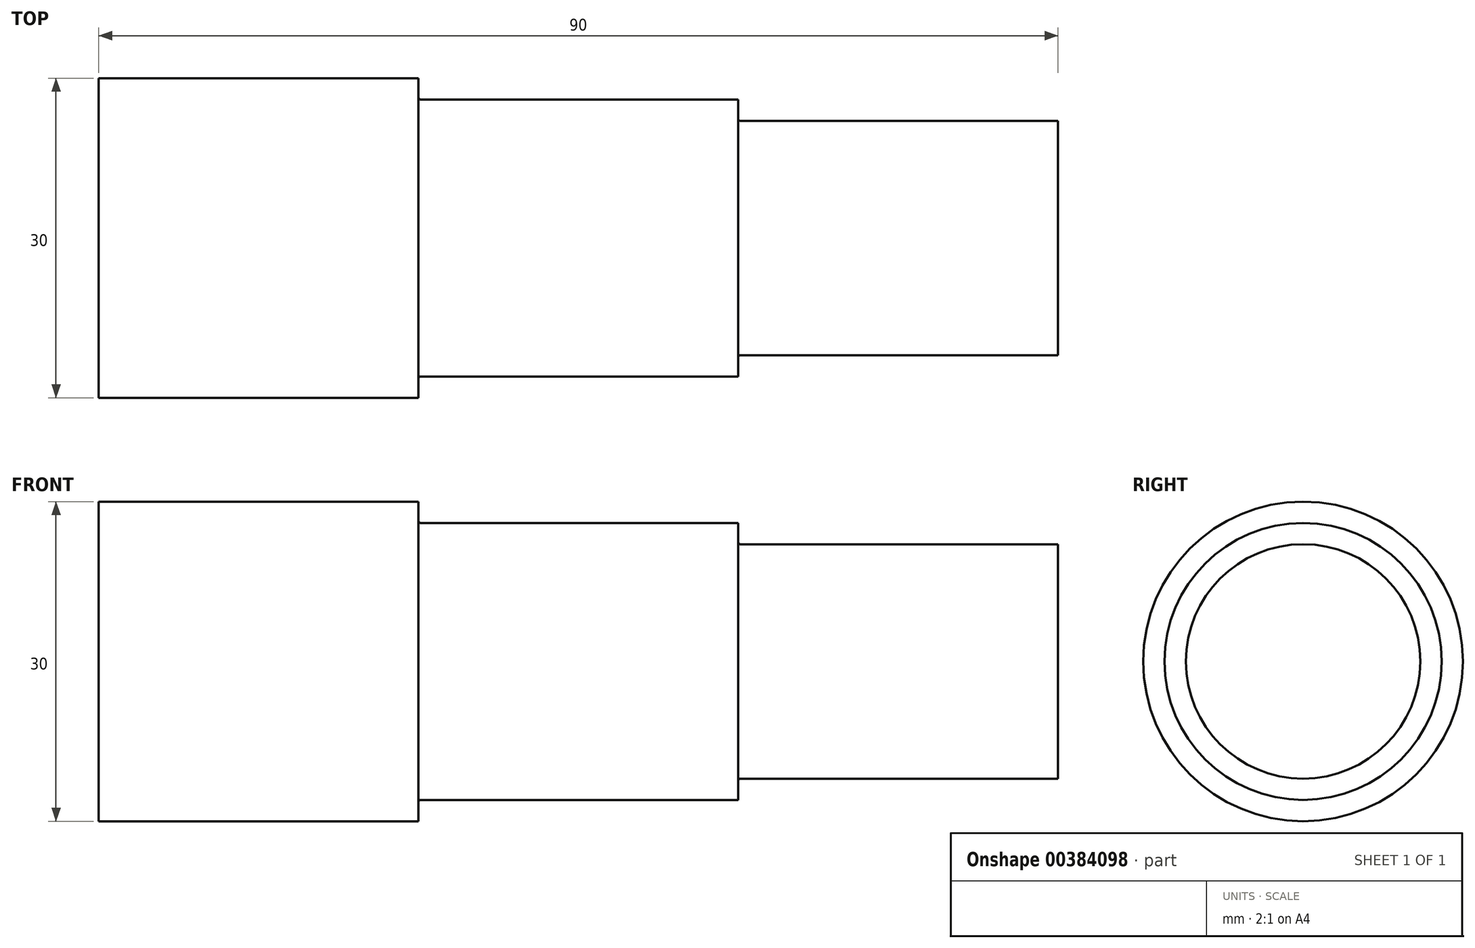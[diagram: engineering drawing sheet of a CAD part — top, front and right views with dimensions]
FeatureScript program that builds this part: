
annotation { "Feature Type Name" : "Feature", "Feature Type Description" : "" }
export const myFeature = defineFeature(function(context is Context, id is Id, definition is map)
    precondition{}
    {
        {
            var Q0;
            Q0=qCreatedBy(makeId("Front.planeOp"),FACE);
            var sketch = newSketch(context, id + "F0", { "sketchPlane" : qUnion([Q0])});
            skLineSegment(sketch, "E0", {"start": v(0, 0) * mm, "end": v(0, 11) * mm});
            skLineSegment(sketch, "E1", {"start": v(0, 11) * mm, "end": v(-29.8, 11) * mm});
            skLineSegment(sketch, "E2", {"start": v(-30, 11.2) * mm, "end": v(-30, 13) * mm});
            skLineSegment(sketch, "E3", {"start": v(-30, 13) * mm, "end": v(-59.8, 13) * mm});
            skLineSegment(sketch, "E4", {"start": v(-60, 13.2) * mm, "end": v(-60, 15) * mm});
            skLineSegment(sketch, "E5", {"start": v(-60, 15) * mm, "end": v(-90, 15) * mm});
            skLineSegment(sketch, "E6", {"start": v(-90, 15) * mm, "end": v(-90, 0) * mm});
            skLineSegment(sketch, "E7", {"start": v(-90, 0) * mm, "end": v(0, 0) * mm});
            skLineSegment(sketch, "E8.MirrorCS", {"start": v(-60, -15) * mm, "end": v(-90, -15) * mm});
            skLineSegment(sketch, "E9.MirrorCS", {"start": v(-90, -15) * mm, "end": v(-90, 0) * mm});
            skLineSegment(sketch, "E10.MirrorCS", {"start": v(-30, -13) * mm, "end": v(-59.8, -13) * mm});
            skLineSegment(sketch, "E11.MirrorCS", {"start": v(0, -11) * mm, "end": v(-29.8, -11) * mm});
            skLineSegment(sketch, "E12.MirrorCS", {"start": v(0, 0) * mm, "end": v(0, -11) * mm});
            skLineSegment(sketch, "E13.MirrorCS", {"start": v(-30, -11.2) * mm, "end": v(-30, -13) * mm});
            skLineSegment(sketch, "E14.MirrorCS", {"start": v(-60, -13.2) * mm, "end": v(-60, -15) * mm});
            skPoint(sketch, "E15.visualSharp", {"position": v(-60, 13) * mm});
            skArc(sketch, "E15.filletArc", {"start": v(-60, 13.2) * mm, "mid": v(-59.94, 13.06) * mm, "end": v(-59.8, 13) * mm});
            skPoint(sketch, "E16.visualSharp", {"position": v(-30, 11) * mm});
            skArc(sketch, "E16.filletArc", {"start": v(-30, 11.2) * mm, "mid": v(-29.94, 11.06) * mm, "end": v(-29.8, 11) * mm});
            skPoint(sketch, "E17.visualSharp", {"position": v(-60, -13) * mm});
            skArc(sketch, "E17.filletArc", {"start": v(-59.8, -13) * mm, "mid": v(-59.94, -13.06) * mm, "end": v(-60, -13.2) * mm});
            skPoint(sketch, "E18.visualSharp", {"position": v(-30, -11) * mm});
            skArc(sketch, "E18.filletArc", {"start": v(-29.8, -11) * mm, "mid": v(-29.94, -11.06) * mm, "end": v(-30, -11.2) * mm});
            skSolve(sketch);
        }
        {
            var Q0;
            Q0=makeQuery(id+"F0.imprint","IMPRINT",FACE,{"disambiguationData":[TD([[makeQuery(id+"F0.imprint","IMPRINT",EDGE,{"derivedFrom":sQuery(id+"F0.wireOp",EDGE,"E0")}),1.0]])]});
            var Q1;
            Q1=sQuery(id+"F0.wireOp",EDGE,"E7");
            revolve(context, id + "F1", {"entities" : qUnion([Q0]), "axis" : qUnion([Q1]), "revolveType" : RevolveType.FULL});
        }
    });
